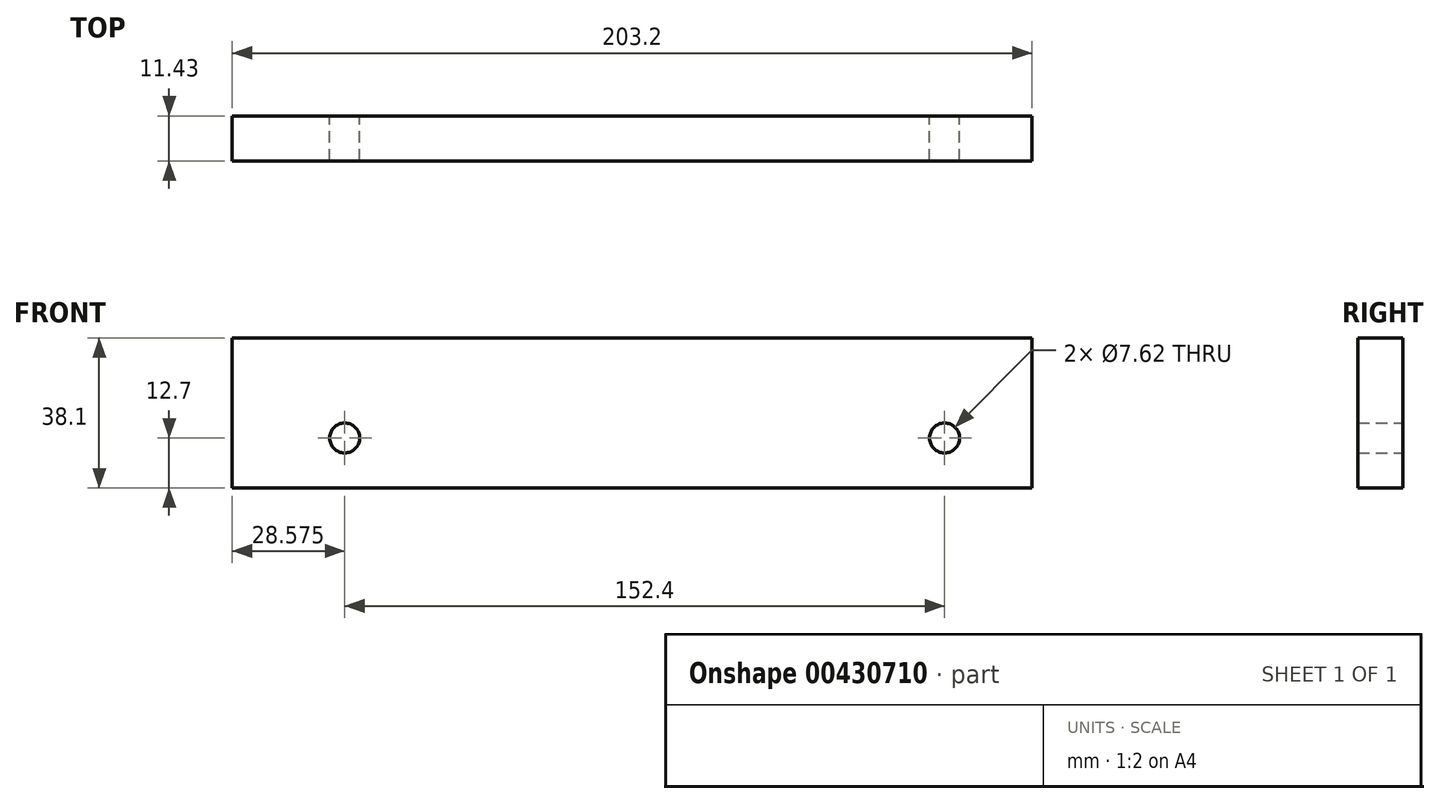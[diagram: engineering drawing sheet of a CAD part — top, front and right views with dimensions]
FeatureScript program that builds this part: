
annotation { "Feature Type Name" : "Feature", "Feature Type Description" : "" }
export const myFeature = defineFeature(function(context is Context, id is Id, definition is map)
    precondition{}
    {
        {
            var Q0;
            Q0=qCreatedBy(makeId("Front.planeOp"),FACE);
            var sketch = newSketch(context, id + "F0", { "sketchPlane" : qUnion([Q0])});
            skLineSegment(sketch, "E0.bottom", {"start": v(0, 0) * mm, "end": v(203.2, 0) * mm});
            skLineSegment(sketch, "E0.top", {"start": v(0, 38.1) * mm, "end": v(203.2, 38.1) * mm});
            skLineSegment(sketch, "E0.left", {"start": v(0, 0) * mm, "end": v(0, 38.1) * mm});
            skLineSegment(sketch, "E0.right", {"start": v(203.2, 0) * mm, "end": v(203.2, 38.1) * mm});
            skCircle(sketch, "E1", {"center": v(28.57, 12.7) * mm, "radius": 3.81 * mm});
            skCircle(sketch, "E2", {"center": v(180.98, 12.7) * mm, "radius": 3.81 * mm});
            skLineSegment(sketch, "E3", {"start": v(28.58, 12.7) * mm, "end": v(180.98, 12.7) * mm, "construction": true});
            skSolve(sketch);
        }
        {
            var Q0;
            Q0=makeQuery(id+"F0.imprint","IMPRINT",FACE,{"disambiguationData":[TD([[makeQuery(id+"F0.imprint","IMPRINT",EDGE,{"derivedFrom":sQuery(id+"F0.wireOp",EDGE,"E0.bottom")}),1.0]])]});
            extrude(context, id + "F1", {"entities" : qUnion([Q0]), "depth" : 11.43 * mm, "offsetDistance" : 25.4 * mm});
        }
    });
